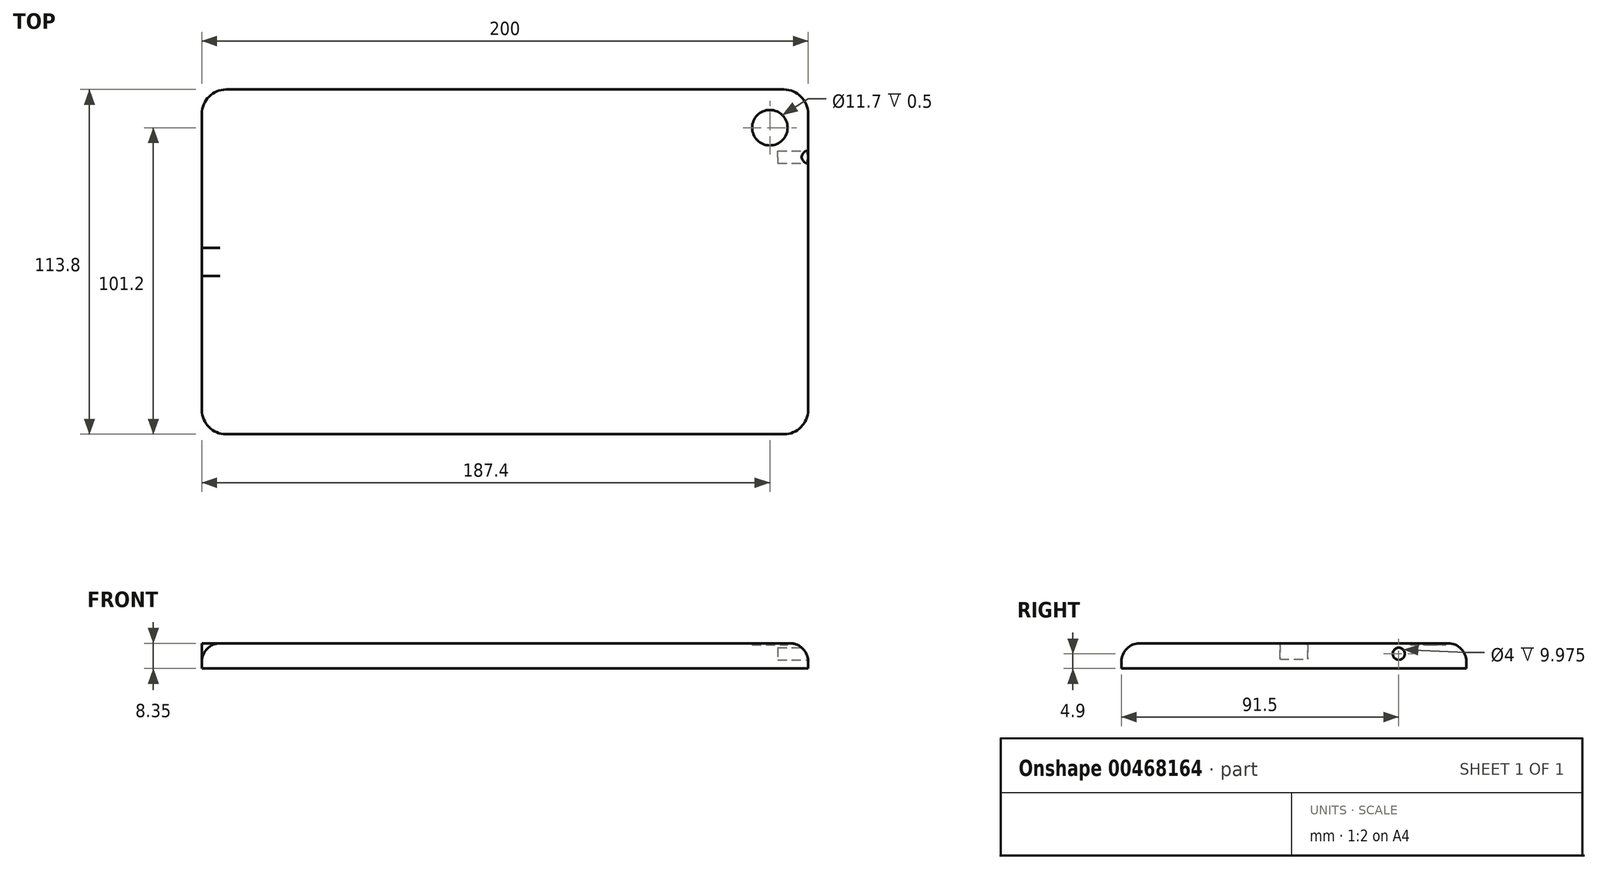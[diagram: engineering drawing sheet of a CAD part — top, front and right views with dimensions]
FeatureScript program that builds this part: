
annotation { "Feature Type Name" : "Feature", "Feature Type Description" : "" }
export const myFeature = defineFeature(function(context is Context, id is Id, definition is map)
    precondition{}
    {
        {
            var Q0;
            Q0=qCreatedBy(makeId("Top.planeOp"),FACE);
            var sketch = newSketch(context, id + "F0", { "sketchPlane" : qUnion([Q0])});
            skLineSegment(sketch, "E0.bottom", {"start": v(100, 56.9) * mm, "end": v(-100, 56.9) * mm});
            skLineSegment(sketch, "E0.top", {"start": v(100, -56.9) * mm, "end": v(-100, -56.9) * mm});
            skLineSegment(sketch, "E0.left", {"start": v(100, 56.9) * mm, "end": v(100, -56.9) * mm});
            skLineSegment(sketch, "E0.right", {"start": v(-100, 56.9) * mm, "end": v(-100, -56.9) * mm});
            skPoint(sketch, "E0.middle", {"position": v(0, 0) * mm});
            skSolve(sketch);
        }
        {
            var Q0;
            Q0=makeQuery(id+"F0.imprint","IMPRINT",FACE,{"disambiguationData":[TD([[makeQuery(id+"F0.imprint","IMPRINT",EDGE,{"derivedFrom":sQuery(id+"F0.wireOp",EDGE,"E0.bottom")}),1.0]])]});
            extrude(context, id + "F1", {"entities" : qUnion([Q0]), "depth" : 8.35 * mm});
        }
        {
            var Q0;
            Q0=makeQuery(id+"F1.opExtrude","SWEPT_EDGE",EDGE,{"disambiguationData":[OSD([sQuery(id+"F0.wireOp",EDGE,"E0.top"),sQuery(id+"F0.wireOp",EDGE,"E0.right")])]});
            var Q1;
            Q1=makeQuery(id+"F1.opExtrude","SWEPT_EDGE",EDGE,{"disambiguationData":[OSD([sQuery(id+"F0.wireOp",EDGE,"E0.top"),sQuery(id+"F0.wireOp",EDGE,"E0.left")])]});
            var Q2;
            Q2=makeQuery(id+"F1.opExtrude","SWEPT_EDGE",EDGE,{"disambiguationData":[OSD([sQuery(id+"F0.wireOp",EDGE,"E0.bottom"),sQuery(id+"F0.wireOp",EDGE,"E0.right")])]});
            var Q3;
            Q3=makeQuery(id+"F1.opExtrude","SWEPT_EDGE",EDGE,{"disambiguationData":[OSD([sQuery(id+"F0.wireOp",EDGE,"E0.bottom"),sQuery(id+"F0.wireOp",EDGE,"E0.left")])]});
            fillet(context, id + "F2", {"entities" : qUnion([Q0, Q1, Q2, Q3]), "radius" : 8 * mm, "tangentPropagation" : true, "allowEdgeOverflow" : false});
        }
        {
            var Q0;
            Q0=makeQuery(id+"F1.opExtrude","CAP_EDGE",EDGE,{"disambiguationData":[OSD([sQuery(id+"F0.wireOp",EDGE,"E0.left")])],"isStart":false});
            fillet(context, id + "F3", {"entities" : qUnion([Q0]), "radius" : 6 * mm, "tangentPropagation" : true, "allowEdgeOverflow" : false});
        }
        {
            var Q0;
            {var subQ0=sQuery(id+"F0.wireOp",EDGE,"E0.right");var subQ1=sQuery(id+"F0.wireOp",EDGE,"E0.top");var subQ2=makeQuery(id+"F1.opExtrude","CAP_FACE",FACE,{"disambiguationData":[OSD([sQuery(id+"F0.wireOp",EDGE,"E0.bottom"),subQ1,sQuery(id+"F0.wireOp",EDGE,"E0.left"),subQ0])],"isStart":false});Q0=makeQuery(id+"F3.opFillet","BLEND_VERTEX",VERTEX,{"blendedFrom":[makeQuery(id+"F2.opFillet","BLEND_EDGE",EDGE,{"blendedFrom":[makeQuery(id+"F1.opExtrude","SWEPT_EDGE",EDGE,{"disambiguationData":[OSD([subQ1,subQ0])]}),subQ2],"blendedInto":[subQ2]}),makeQuery(id+"F1.opExtrude","CAP_EDGE",EDGE,{"disambiguationData":[OSD([subQ1])],"isStart":false}),subQ2],"blendedInto":[subQ2]});}
            var Q1;
            {var subQ0=sQuery(id+"F0.wireOp",EDGE,"E0.left");var subQ1=sQuery(id+"F0.wireOp",EDGE,"E0.top");var subQ2=makeQuery(id+"F1.opExtrude","CAP_FACE",FACE,{"disambiguationData":[OSD([sQuery(id+"F0.wireOp",EDGE,"E0.bottom"),subQ1,subQ0,sQuery(id+"F0.wireOp",EDGE,"E0.right")])],"isStart":false});Q1=makeQuery(id+"F3.opFillet","BLEND_VERTEX",VERTEX,{"blendedFrom":[makeQuery(id+"F2.opFillet","BLEND_EDGE",EDGE,{"blendedFrom":[makeQuery(id+"F1.opExtrude","SWEPT_EDGE",EDGE,{"disambiguationData":[OSD([subQ1,subQ0])]}),subQ2],"blendedInto":[subQ2]}),makeQuery(id+"F1.opExtrude","CAP_EDGE",EDGE,{"disambiguationData":[OSD([subQ1])],"isStart":false}),subQ2],"blendedInto":[subQ2]});}
            var Q2;
            {var subQ0=sQuery(id+"F0.wireOp",EDGE,"E0.left");var subQ1=sQuery(id+"F0.wireOp",EDGE,"E0.bottom");var subQ2=makeQuery(id+"F1.opExtrude","CAP_FACE",FACE,{"disambiguationData":[OSD([subQ1,sQuery(id+"F0.wireOp",EDGE,"E0.top"),subQ0,sQuery(id+"F0.wireOp",EDGE,"E0.right")])],"isStart":false});Q2=makeQuery(id+"F3.opFillet","BLEND_VERTEX",VERTEX,{"blendedFrom":[makeQuery(id+"F2.opFillet","BLEND_EDGE",EDGE,{"blendedFrom":[makeQuery(id+"F1.opExtrude","SWEPT_EDGE",EDGE,{"disambiguationData":[OSD([subQ1,subQ0])]}),subQ2],"blendedInto":[subQ2]}),makeQuery(id+"F1.opExtrude","CAP_EDGE",EDGE,{"disambiguationData":[OSD([subQ1])],"isStart":false}),subQ2],"blendedInto":[subQ2]});}
            cPlane(context, id + "F4", {"entities" : qUnion([Q0, Q1, Q2]), "cplaneType" : CPlaneType.THREE_POINT, "offset" : 25 * mm, "width" : 150 * mm, "height" : 150 * mm});
        }
        {
            var Q0;
            Q0=qCreatedBy(id+"F4.planeOp",FACE);
            var sketch = newSketch(context, id + "F5", { "sketchPlane" : qUnion([Q0])});
            skLineSegment(sketch, "E1.0", {"start": v(-92, -56.9) * mm, "end": v(92, -56.9) * mm, "construction": true});
            skLineSegment(sketch, "E2.0", {"start": v(100, -48.9) * mm, "end": v(100, 48.9) * mm, "construction": true});
            skCircle(sketch, "E3", {"center": v(87.4, -44.3) * mm, "radius": 5.85 * mm});
            skSolve(sketch);
        }
        {
            var Q0;
            Q0=makeQuery(id+"F5.imprint","IMPRINT",FACE,{"disambiguationData":[TD([[makeQuery(id+"F5.imprint","IMPRINT",EDGE,{"derivedFrom":sQuery(id+"F5.wireOp",EDGE,"E3")}),1.0]])]});
            var Q1;
            Q1=sQuery(id+"F5.wireOp",EDGE,"E3");
            extrude(context, id + "F6", {"entities" : qUnion([Q0]), "operationType" : NewBodyOperationType.REMOVE, "surfaceEntities" : qUnion([Q1]), "depth" : 0.5 * mm});
        }
        {
            var Q0;
            {var subQ0=sQuery(id+"F0.wireOp",EDGE,"E0.left");var subQ1=sQuery(id+"F0.wireOp",EDGE,"E0.top");Q0=makeQuery(id+"F3.opFillet","BLEND_VERTEX",VERTEX,{"blendedFrom":[makeQuery(id+"F2.opFillet","BLEND_EDGE",EDGE,{"blendedFrom":[makeQuery(id+"F1.opExtrude","SWEPT_EDGE",EDGE,{"disambiguationData":[OSD([subQ1,subQ0])]}),makeQuery(id+"F1.opExtrude","CAP_FACE",FACE,{"disambiguationData":[OSD([sQuery(id+"F0.wireOp",EDGE,"E0.bottom"),subQ1,subQ0,sQuery(id+"F0.wireOp",EDGE,"E0.right")])],"isStart":false})],"blendedInto":[makeQuery(id+"F1.opExtrude","CAP_FACE",FACE,{"disambiguationData":[OSD([sQuery(id+"F0.wireOp",EDGE,"E0.bottom"),subQ1,subQ0,sQuery(id+"F0.wireOp",EDGE,"E0.right")])],"isStart":false})]}),makeQuery(id+"F1.opExtrude","CAP_EDGE",EDGE,{"disambiguationData":[OSD([subQ0])],"isStart":false}),makeQuery(id+"F2.opFillet","BLEND_FACE",FACE,{"disambiguationData":[OSD([subQ1,subQ0])]}),makeQuery(id+"F1.opExtrude","SWEPT_FACE",FACE,{"disambiguationData":[OSD([subQ0])]})],"blendedInto":[makeQuery(id+"F2.opFillet","BLEND_FACE",FACE,{"disambiguationData":[OSD([subQ1,subQ0])]}),makeQuery(id+"F1.opExtrude","SWEPT_FACE",FACE,{"disambiguationData":[OSD([subQ0])]})]});}
            var Q1;
            {var subQ0=sQuery(id+"F0.wireOp",EDGE,"E0.left");var subQ1=sQuery(id+"F0.wireOp",EDGE,"E0.top");Q1=makeQuery(id+"F2.opFillet","BLEND_VERTEX",VERTEX,{"blendedFrom":[makeQuery(id+"F1.opExtrude","SWEPT_EDGE",EDGE,{"disambiguationData":[OSD([subQ1,subQ0])]}),makeQuery(id+"F1.opExtrude","CAP_FACE",FACE,{"disambiguationData":[OSD([sQuery(id+"F0.wireOp",EDGE,"E0.bottom"),subQ1,subQ0,sQuery(id+"F0.wireOp",EDGE,"E0.right")])],"isStart":true}),makeQuery(id+"F1.opExtrude","SWEPT_FACE",FACE,{"disambiguationData":[OSD([subQ0])]})],"blendedInto":[makeQuery(id+"F1.opExtrude","CAP_FACE",FACE,{"disambiguationData":[OSD([sQuery(id+"F0.wireOp",EDGE,"E0.bottom"),subQ1,subQ0,sQuery(id+"F0.wireOp",EDGE,"E0.right")])],"isStart":true}),makeQuery(id+"F1.opExtrude","SWEPT_FACE",FACE,{"disambiguationData":[OSD([subQ0])]})]});}
            var Q2;
            {var subQ0=sQuery(id+"F0.wireOp",EDGE,"E0.left");var subQ1=sQuery(id+"F0.wireOp",EDGE,"E0.bottom");Q2=makeQuery(id+"F3.opFillet","BLEND_VERTEX",VERTEX,{"blendedFrom":[makeQuery(id+"F2.opFillet","BLEND_EDGE",EDGE,{"blendedFrom":[makeQuery(id+"F1.opExtrude","SWEPT_EDGE",EDGE,{"disambiguationData":[OSD([subQ1,subQ0])]}),makeQuery(id+"F1.opExtrude","CAP_FACE",FACE,{"disambiguationData":[OSD([subQ1,sQuery(id+"F0.wireOp",EDGE,"E0.top"),subQ0,sQuery(id+"F0.wireOp",EDGE,"E0.right")])],"isStart":false})],"blendedInto":[makeQuery(id+"F1.opExtrude","CAP_FACE",FACE,{"disambiguationData":[OSD([subQ1,sQuery(id+"F0.wireOp",EDGE,"E0.top"),subQ0,sQuery(id+"F0.wireOp",EDGE,"E0.right")])],"isStart":false})]}),makeQuery(id+"F1.opExtrude","CAP_EDGE",EDGE,{"disambiguationData":[OSD([subQ0])],"isStart":false}),makeQuery(id+"F2.opFillet","BLEND_FACE",FACE,{"disambiguationData":[OSD([subQ1,subQ0])]}),makeQuery(id+"F1.opExtrude","SWEPT_FACE",FACE,{"disambiguationData":[OSD([subQ0])]})],"blendedInto":[makeQuery(id+"F2.opFillet","BLEND_FACE",FACE,{"disambiguationData":[OSD([subQ1,subQ0])]}),makeQuery(id+"F1.opExtrude","SWEPT_FACE",FACE,{"disambiguationData":[OSD([subQ0])]})]});}
            cPlane(context, id + "F7", {"entities" : qUnion([Q0, Q1, Q2]), "cplaneType" : CPlaneType.THREE_POINT, "offset" : 25 * mm, "width" : 150 * mm, "height" : 150 * mm});
        }
        {
            var Q0;
            Q0=qCreatedBy(id+"F7.planeOp",FACE);
            var sketch = newSketch(context, id + "F8", { "sketchPlane" : qUnion([Q0])});
            skCircle(sketch, "E4", {"center": v(-34.6, 4.9) * mm, "radius": 2 * mm});
            skSolve(sketch);
        }
        {
            var Q0;
            Q0=makeQuery(id+"F8.imprint","IMPRINT",FACE,{"disambiguationData":[TD([[makeQuery(id+"F8.imprint","IMPRINT",EDGE,{"derivedFrom":sQuery(id+"F8.wireOp",EDGE,"E4")}),1.0]])]});
            extrude(context, id + "F9", {"entities" : qUnion([Q0]), "operationType" : NewBodyOperationType.REMOVE, "depth" : 10 * mm});
        }
        {
            var Q0;
            {var subQ0=sQuery(id+"F0.wireOp",EDGE,"E0.right");Q0=makeQuery(id+"F3.opFillet","BLEND_EDGE",EDGE,{"blendedFrom":[makeQuery(id+"F1.opExtrude","CAP_EDGE",EDGE,{"disambiguationData":[OSD([subQ0])],"isStart":false}),makeQuery(id+"F1.opExtrude","SWEPT_FACE",FACE,{"disambiguationData":[OSD([subQ0])]})],"blendedInto":[makeQuery(id+"F1.opExtrude","SWEPT_FACE",FACE,{"disambiguationData":[OSD([subQ0])]})]});}
            cPoint(context, id + "F10", {"entities" : qUnion([Q0]), "parameter" : 0.5});
        }
        {
            var Q0;
            {var subQ0=sQuery(id+"F0.wireOp",EDGE,"E0.right");var subQ1=sQuery(id+"F0.wireOp",EDGE,"E0.top");Q0=makeQuery(id+"F2.opFillet","BLEND_VERTEX",VERTEX,{"blendedFrom":[makeQuery(id+"F1.opExtrude","SWEPT_EDGE",EDGE,{"disambiguationData":[OSD([subQ1,subQ0])]}),makeQuery(id+"F1.opExtrude","CAP_FACE",FACE,{"disambiguationData":[OSD([sQuery(id+"F0.wireOp",EDGE,"E0.bottom"),subQ1,sQuery(id+"F0.wireOp",EDGE,"E0.left"),subQ0])],"isStart":true}),makeQuery(id+"F1.opExtrude","SWEPT_FACE",FACE,{"disambiguationData":[OSD([subQ0])]})],"blendedInto":[makeQuery(id+"F1.opExtrude","CAP_FACE",FACE,{"disambiguationData":[OSD([sQuery(id+"F0.wireOp",EDGE,"E0.bottom"),subQ1,sQuery(id+"F0.wireOp",EDGE,"E0.left"),subQ0])],"isStart":true}),makeQuery(id+"F1.opExtrude","SWEPT_FACE",FACE,{"disambiguationData":[OSD([subQ0])]})]});}
            var Q1;
            {var subQ0=sQuery(id+"F0.wireOp",EDGE,"E0.right");var subQ1=sQuery(id+"F0.wireOp",EDGE,"E0.top");Q1=makeQuery(id+"F3.opFillet","BLEND_VERTEX",VERTEX,{"blendedFrom":[makeQuery(id+"F2.opFillet","BLEND_EDGE",EDGE,{"blendedFrom":[makeQuery(id+"F1.opExtrude","SWEPT_EDGE",EDGE,{"disambiguationData":[OSD([subQ1,subQ0])]}),makeQuery(id+"F1.opExtrude","CAP_FACE",FACE,{"disambiguationData":[OSD([sQuery(id+"F0.wireOp",EDGE,"E0.bottom"),subQ1,sQuery(id+"F0.wireOp",EDGE,"E0.left"),subQ0])],"isStart":false})],"blendedInto":[makeQuery(id+"F1.opExtrude","CAP_FACE",FACE,{"disambiguationData":[OSD([sQuery(id+"F0.wireOp",EDGE,"E0.bottom"),subQ1,sQuery(id+"F0.wireOp",EDGE,"E0.left"),subQ0])],"isStart":false})]}),makeQuery(id+"F1.opExtrude","CAP_EDGE",EDGE,{"disambiguationData":[OSD([subQ0])],"isStart":false}),makeQuery(id+"F2.opFillet","BLEND_FACE",FACE,{"disambiguationData":[OSD([subQ1,subQ0])]}),makeQuery(id+"F1.opExtrude","SWEPT_FACE",FACE,{"disambiguationData":[OSD([subQ0])]})],"blendedInto":[makeQuery(id+"F2.opFillet","BLEND_FACE",FACE,{"disambiguationData":[OSD([subQ1,subQ0])]}),makeQuery(id+"F1.opExtrude","SWEPT_FACE",FACE,{"disambiguationData":[OSD([subQ0])]})]});}
            var Q2;
            Q2 = qCreatedBy(id + "F10" ,VERTEX);
            cPlane(context, id + "F11", {"entities" : qUnion([Q0, Q1, Q2]), "cplaneType" : CPlaneType.THREE_POINT, "offset" : 25 * mm, "width" : 150 * mm, "height" : 150 * mm});
        }
        {
            var Q0;
            Q0=qCreatedBy(id+"F11.planeOp",FACE);
            var sketch = newSketch(context, id + "F12", { "sketchPlane" : qUnion([Q0])});
            skLineSegment(sketch, "E5.0", {"start": v(48.9, 8.35) * mm, "end": v(-48.9, 8.35) * mm, "construction": true});
            skLineSegment(sketch, "E6.0", {"start": v(48.9, 0) * mm, "end": v(-48.9, 0) * mm, "construction": true});
            skLineSegment(sketch, "E7", {"start": v(0, 8.35) * mm, "end": v(0, 0) * mm, "construction": true});
            skLineSegment(sketch, "E8.bottom", {"start": v(-4.6, 8.35) * mm, "end": v(4.6, 8.35) * mm});
            skLineSegment(sketch, "E8.top", {"start": v(-4.6, 3.05) * mm, "end": v(4.6, 3.05) * mm});
            skLineSegment(sketch, "E8.left", {"start": v(-4.6, 8.35) * mm, "end": v(-4.6, 3.05) * mm});
            skLineSegment(sketch, "E8.right", {"start": v(4.6, 8.35) * mm, "end": v(4.6, 3.05) * mm});
            skPoint(sketch, "E8.middle", {"position": v(0, 4.65) * mm});
            skPoint(sketch, "E9", {"position": v(0, 8.35) * mm});
            skSolve(sketch);
        }
        {
            var Q0;
            Q0=makeQuery(id+"F12.imprint","IMPRINT",FACE,{"disambiguationData":[TD([[makeQuery(id+"F12.imprint","IMPRINT",EDGE,{"derivedFrom":sQuery(id+"F12.wireOp",EDGE,"E8.bottom")}),-1.0]])]});
            extrude(context, id + "F13", {"entities" : qUnion([Q0]), "operationType" : NewBodyOperationType.ADD, "depth" : 25 * mm});
        }
    });
